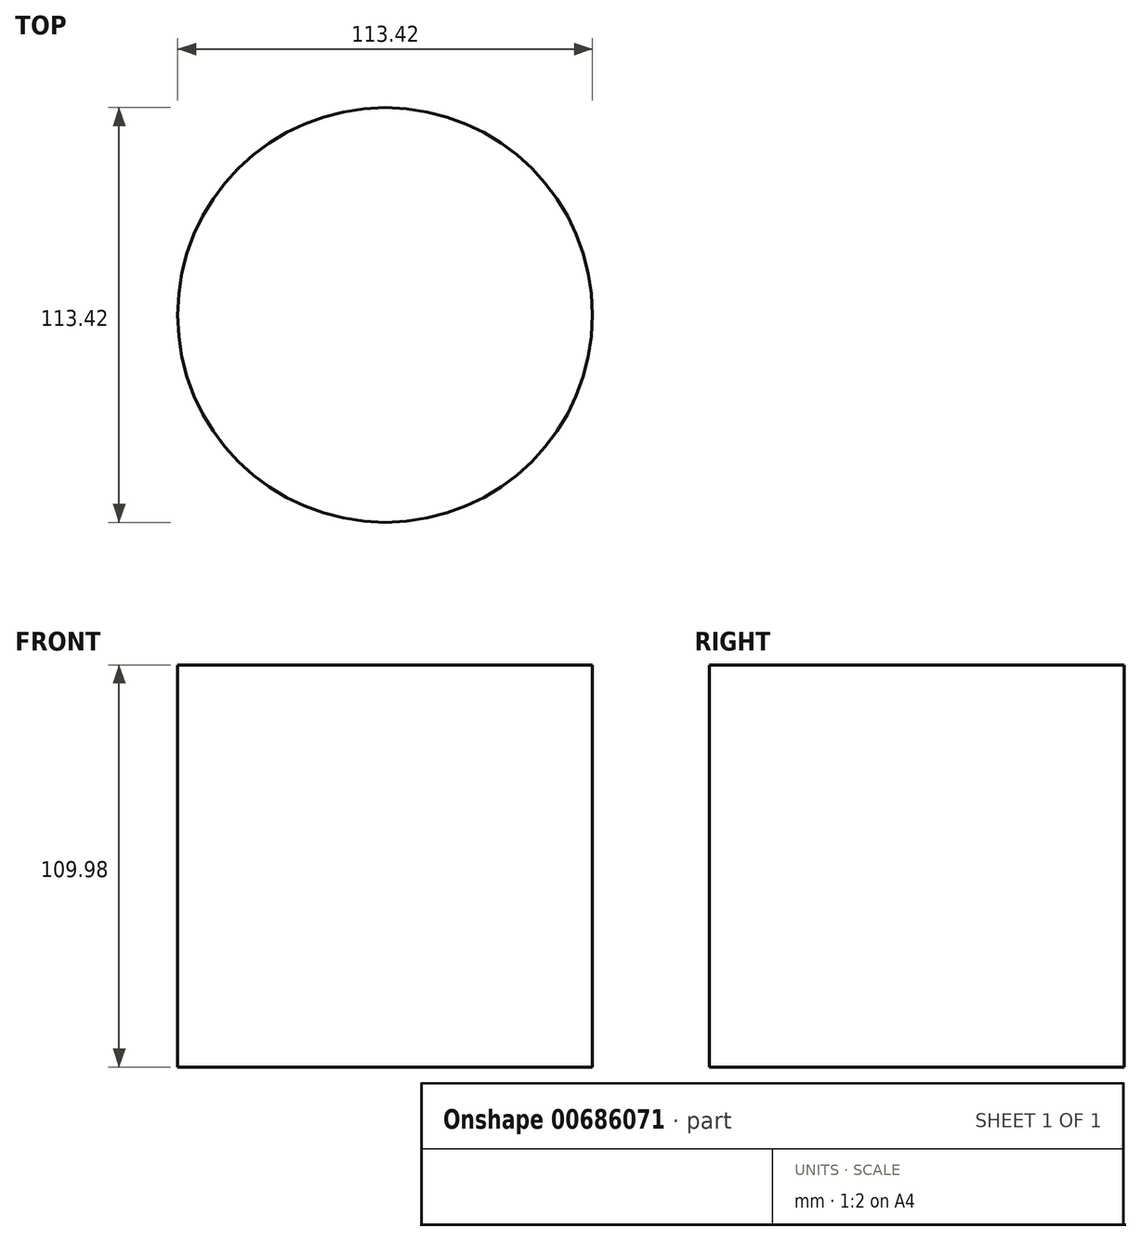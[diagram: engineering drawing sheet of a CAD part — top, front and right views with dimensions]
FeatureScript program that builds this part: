
annotation { "Feature Type Name" : "Feature", "Feature Type Description" : "" }
export const myFeature = defineFeature(function(context is Context, id is Id, definition is map)
    precondition{}
    {
        {
            var Q0;
            Q0=qCreatedBy(makeId("Top.planeOp"),FACE);
            var sketch = newSketch(context, id + "F0", { "sketchPlane" : qUnion([Q0])});
            skCircle(sketch, "E0", {"center": v(0, 0) * mm, "radius": 56.7 * mm});
            skSolve(sketch);
        }
        {
            var Q0;
            Q0 = qSketchRegion(id + "F0", true);
            extrude(context, id + "F1", {"entities" : qUnion([Q0]), "depth" : 109.98 * mm, "offsetDistance" : 25.4 * mm});
        }
        {
            var Q0;
            Q0=qCreatedBy(makeId("Right.planeOp"),FACE);
            var sketch = newSketch(context, id + "F2", { "sketchPlane" : qUnion([Q0])});
            skArc(sketch, "E1", {"start": v(-56.57, 42.46) * mm, "mid": v(-82.28, 21.23) * mm, "end": v(-56.57, 0) * mm});
            skArc(sketch, "E2", {"start": v(56.77, 0) * mm, "mid": v(82.79, 19.95) * mm, "end": v(57.56, 40.88) * mm});
            skSolve(sketch);
        }
        {
            var Q0;
            Q0=sQuery(id+"F2.wireOp",EDGE,"E2");
            extrude(context, id + "F3", {"bodyType" : ToolBodyType.SURFACE, "surfaceEntities" : qUnion([Q0]), "depth" : 25.4 * mm, "offsetDistance" : 25.4 * mm});
        }
    });
